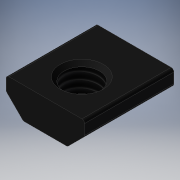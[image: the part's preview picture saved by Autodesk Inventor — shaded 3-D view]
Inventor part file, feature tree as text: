
AUTODESK INVENTOR PART (.ipt)
format: ipt  version: 2019 (Build 230136000, 136)  size: 143,360 bytes
history: native  units: mm
features: other x7, sketch x2, extrude x1, revolve x1, thread x1
ambient origin geometry x8: Origin, YZ Plane, XZ Plane, XY Plane, X Axis, Y Axis, Z Axis, Center Point
bodies: Solid1 (feature_tree)
feature tree (12):
  extrude  "Extrusion1"  TaperAngle=360.0deg  [1 undecoded]
  revolve  "Revolution1"  [1 undecoded]
  thread  "Thread1"  [1 undecoded]
  other  "tnut_XY"
  other  "tnut_YZ"
  other  "tnut_ZX"
  other  "tnut_X"
  other  "tnut_Y"
  other  "tnut_Z"
  other  "tnut_Center"
  sketch  "Sketch_1"  dims[d0=12.446mm d1=0.0mm d2=360.0deg]
  sketch  "Sketch_4"  dims[d3=3.2604mm d4=0.0mm d5=0.0mm]
note: 3 required parameter values undecoded (feature->parameter linkage not recoverable at this tier; creation-order binding heuristic only, values carry confidence <= 0.55)